FCSTD DOCUMENT  (FreeCAD 0.18R16131 (Git))
Label: Blinds
License: All rights reserved
LicenseURL: http://en.wikipedia.org/wiki/All_rights_reserved
objects: App::Part×2, Sketcher::SketchObject×2
note: 2 computed .brp shape members not serialized (recipe doc carries the construction recipe); baked Part::Feature solids carry a one-line shape summary decoded from their .brp

FEATURE [App::Part] Part
  Origin = -> Origin
FEATURE [Sketcher::SketchObject] Sketch
  sketch-geometry (54):
    g0: LineSegment StartX=-75.9771 StartY=43.0234 StartZ=0 EndX=-55.9771 EndY=43.0234 EndZ=0
    g1: LineSegment StartX=-75.9771 StartY=43.0234 StartZ=0 EndX=-75.9771 EndY=33.0234 EndZ=0
    g2: LineSegment StartX=-55.9771 StartY=43.0234 StartZ=0 EndX=-55.9771 EndY=33.0234 EndZ=0
    g3: LineSegment StartX=-75.9771 StartY=33.0234 StartZ=0 EndX=-85.9771 EndY=33.0234 EndZ=0
    g4: LineSegment StartX=-85.9771 StartY=33.0234 StartZ=0 EndX=-85.9771 EndY=25.0234 EndZ=0
    g5: LineSegment StartX=-35.9771 StartY=33.0234 StartZ=0 EndX=-55.9771 EndY=33.0234 EndZ=0
    g6: Circle CenterX=-71.9771 CenterY=37.6234 CenterZ=0 NormalX=0 NormalY=0 NormalZ=1 AngleXU=0 Radius=1.6
    g7: Circle CenterX=-59.9771 CenterY=37.6234 CenterZ=0 NormalX=0 NormalY=0 NormalZ=1 AngleXU=0 Radius=1.6
    g8: Circle CenterX=-39.9771 CenterY=29.0234 CenterZ=0 NormalX=0 NormalY=0 NormalZ=1 AngleXU=0 Radius=2.2
    g9: LineSegment StartX=-35.9771 StartY=33.0234 StartZ=0 EndX=-35.9771 EndY=29.0234 EndZ=0
    g10: LineSegment StartX=-85.9771 StartY=25.0234 StartZ=0 EndX=-39.9771 EndY=25.0234 EndZ=0
    g11: ArcOfCircle CenterX=-39.9771 CenterY=29.0234 CenterZ=0 NormalX=0 NormalY=0 NormalZ=1 AngleXU=0 Radius=4 StartAngle=4.71239 EndAngle=6.28319
    g12: LineSegment StartX=-29.5565 StartY=104.387 StartZ=0 EndX=-29.5565 EndY=99.3874 EndZ=0
    g13: LineSegment StartX=-29.5565 StartY=104.387 StartZ=0 EndX=-151.456 EndY=104.387 EndZ=0
    g14: LineSegment StartX=-151.456 StartY=104.387 StartZ=0 EndX=-151.456 EndY=101.387 EndZ=0
    g15: LineSegment StartX=-151.456 StartY=101.387 StartZ=0 EndX=-146.456 EndY=101.387 EndZ=0
    g16: LineSegment StartX=-146.456 StartY=101.387 StartZ=0 EndX=-146.456 EndY=98.3874 EndZ=0
    g17: LineSegment StartX=-146.456 StartY=98.3874 StartZ=0 EndX=-154.456 EndY=98.3874 EndZ=0
    g18: LineSegment StartX=-154.456 StartY=98.3874 StartZ=0 EndX=-154.456 EndY=104.387 EndZ=0
    g19: LineSegment StartX=-154.456 StartY=104.387 StartZ=0 EndX=-241.456 EndY=104.387 EndZ=0
    g20: LineSegment StartX=-241.456 StartY=104.387 StartZ=0 EndX=-241.456 EndY=101.387 EndZ=0
    g21: LineSegment StartX=-241.456 StartY=101.387 StartZ=0 EndX=-236.456 EndY=101.387 EndZ=0
    g22: LineSegment StartX=-236.456 StartY=101.387 StartZ=0 EndX=-236.456 EndY=98.3874 EndZ=0
    g23: LineSegment StartX=-236.456 StartY=98.3874 StartZ=0 EndX=-244.456 EndY=98.3874 EndZ=0
    g24: LineSegment StartX=-244.456 StartY=98.3874 StartZ=0 EndX=-244.456 EndY=104.387 EndZ=0
    g25: LineSegment StartX=-244.456 StartY=104.387 StartZ=0 EndX=-359.556 EndY=104.387 EndZ=0
    g26: LineSegment StartX=-359.556 StartY=104.387 StartZ=0 EndX=-359.556 EndY=99.3874 EndZ=0
    g27: LineSegment StartX=-279.556 StartY=39.3874 StartZ=0 EndX=-109.556 EndY=39.3874 EndZ=0
    g28: LineSegment StartX=-241.456 StartY=95.3874 StartZ=0 EndX=-241.456 EndY=85.3874 EndZ=0
    g29: LineSegment StartX=-241.456 StartY=95.3874 StartZ=0 EndX=-244.456 EndY=95.3874 EndZ=0
    g30: LineSegment StartX=-244.456 StartY=95.3874 StartZ=0 EndX=-244.456 EndY=85.3874 EndZ=0
    g31: LineSegment StartX=-241.456 StartY=85.3874 StartZ=0 EndX=-244.456 EndY=85.3874 EndZ=0
    g32: LineSegment StartX=-154.456 StartY=95.3874 StartZ=0 EndX=-154.456 EndY=85.3874 EndZ=0
    g33: LineSegment StartX=-154.456 StartY=95.3874 StartZ=0 EndX=-151.456 EndY=95.3874 EndZ=0
    g34: LineSegment StartX=-151.456 StartY=95.3874 StartZ=0 EndX=-151.456 EndY=85.3874 EndZ=0
    g35: LineSegment StartX=-154.456 StartY=85.3874 StartZ=0 EndX=-151.456 EndY=85.3874 EndZ=0
    g36: Circle CenterX=-276.556 CenterY=42.3874 CenterZ=0 NormalX=0 NormalY=0 NormalZ=1 AngleXU=0 Radius=1.6
    g37: Circle CenterX=-216.556 CenterY=42.3874 CenterZ=0 NormalX=0 NormalY=0 NormalZ=1 AngleXU=0 Radius=1.6
    g38: Circle CenterX=-172.556 CenterY=42.3874 CenterZ=0 NormalX=0 NormalY=0 NormalZ=1 AngleXU=0 Radius=1.6
    g39: Circle CenterX=-112.556 CenterY=42.3874 CenterZ=0 NormalX=0 NormalY=0 NormalZ=1 AngleXU=0 Radius=1.6
    g40: LineSegment StartX=-54.0017 StartY=76.5916 StartZ=0 EndX=-54.0017 EndY=70.5916 EndZ=0
    g41: LineSegment StartX=-54.0017 StartY=76.5916 StartZ=0 EndX=-48.0017 EndY=76.5916 EndZ=0
    g42: LineSegment StartX=-48.0017 StartY=76.5916 StartZ=0 EndX=-48.0017 EndY=57.5916 EndZ=0
    g43: LineSegment StartX=-48.0017 StartY=57.5916 StartZ=0 EndX=-54.0017 EndY=57.5916 EndZ=0
    g44: LineSegment StartX=-54.0017 StartY=57.5916 StartZ=0 EndX=-54.0017 EndY=67.5916 EndZ=0
    g45: LineSegment StartX=-54.0017 StartY=67.5916 StartZ=0 EndX=-51.0017 EndY=67.5916 EndZ=0
    g46: LineSegment StartX=-51.0017 StartY=67.5916 StartZ=0 EndX=-51.0017 EndY=70.5916 EndZ=0
    g47: LineSegment StartX=-51.0017 StartY=70.5916 StartZ=0 EndX=-54.0017 EndY=70.5916 EndZ=0
    g48: LineSegment StartX=-359.556 StartY=99.3874 StartZ=0 EndX=-319.556 EndY=99.3874 EndZ=0
    g49: LineSegment StartX=-279.556 StartY=64.3874 StartZ=0 EndX=-279.556 EndY=39.3874 EndZ=0
    g50: ArcOfCircle CenterX=-319.243 CenterY=59.3886 CenterZ=0 NormalX=0 NormalY=0 NormalZ=1 AngleXU=0 Radius=40 StartAngle=0.125297 EndAngle=1.57864
    g51: LineSegment StartX=-29.5565 StartY=99.3874 StartZ=0 EndX=-69.5565 EndY=99.3874 EndZ=0
    g52: LineSegment StartX=-109.556 StartY=64.3874 StartZ=0 EndX=-109.556 EndY=39.3874 EndZ=0
    g53: ArcOfCircle CenterX=-69.8701 CenterY=59.3886 CenterZ=0 NormalX=0 NormalY=0 NormalZ=1 AngleXU=0 Radius=40 StartAngle=1.56296 EndAngle=3.0163
  constraints (159):
    c: Coincident(g3,g1)
    c: Coincident(g0,g1)
    c: Coincident(g0,g2)
    c: Coincident(g2,g5)
    c: Coincident(g3,g4)
    c: Parallel(g2,g1)
    c: Parallel(g1,g4)
    c: DistanceY(g1,g2) = 0
    c: DistanceY(g4,g4) = 8
    c: DistanceY(g1,g1) = 10
    c: DistanceX(g3,g3) = 10
    c: DistanceX(g5,g5) = 20
    c: DistanceX(g0,g0) = 20
    c: Radius(g6) = 1.6
    c: Equal(g6,g7)
    c: DistanceY(g6,g7) = 0
    c: Radius(g8) = 2.2
    c: DistanceX(g8,g5) = 4
    c: DistanceY(g8,g5) = 4
    c: DistanceY(g1,g6) = 4.6
    c: DistanceX(g1,g6) = 4
    c: DistanceX(g7,g2) = 4
    c: Coincident(g5,g9)
    c: Coincident(g4,g10)
    c: Angle(g10) = 0
    c: Perpendicular(g4,g10)
    c: Parallel(g4,g9)
    c: Coincident(g10,g11)
    c: Parallel(g10,g0)
    c: Parallel(g0,g3)
    c: Parallel(g3,g5)
    c: Coincident(g9,g11)
    c: DistanceY(g9,g9) = 4
    c: DistanceX(g10,g10) = 46
    c: Radius(g11) = 4
    c: Angle(g27) = 0
    c: Coincident(g13,g12)
    c: Coincident(g14,g13)
    c: Coincident(g14,g15)
    c: Coincident(g15,g16)
    c: Coincident(g16,g17)
    c: Coincident(g18,g17)
    c: Coincident(g18,g19)
    c: Coincident(g20,g19)
    c: Coincident(g20,g21)
    c: Coincident(g21,g22)
    c: Coincident(g23,g22)
    c: Coincident(g23,g24)
    c: Coincident(g24,g25)
    c: Coincident(g25,g26)
    c: Coincident(g29,g28)
    c: Coincident(g29,g30)
    c: Coincident(g31,g30)
    c: Coincident(g31,g28)
    c: Coincident(g35,g32)
    c: Coincident(g35,g34)
    c: Coincident(g33,g32)
    c: Coincident(g33,g34)
    c: Perpendicular(g12,g27)
    c: Parallel(g27,g35)
    c: Parallel(g35,g33)
    c: Parallel(g33,g31)
    c: Parallel(g31,g29)
    c: Parallel(g29,g17)
    c: Parallel(g17,g15)
    c: Parallel(g15,g13)
    c: Parallel(g13,g19)
    c: Parallel(g19,g23)
    c: Parallel(g23,g21)
    c: Parallel(g21,g25)
    c: Parallel(g12,g34)
    c: Parallel(g34,g32)
    c: Parallel(g32,g16)
    c: Parallel(g16,g14)
    c: Parallel(g14,g18)
    c: Parallel(g18,g22)
    c: Parallel(g22,g20)
    c: Parallel(g20,g24)
    c: Parallel(g24,g30)
    c: Parallel(g30,g28)
    c: Parallel(g28,g26)
    c: DistanceX(g27,g12) = 80
    c: DistanceX(g26,g27) = 80
    c: DistanceX(g25,g12) = 330
    c: DistanceY(g12,g12) = 5
    c: DistanceY(g26,g26) = 5
    c: DistanceY(g24,g19) = 0
    c: DistanceY(g18,g13) = 0
    c: DistanceY(g20,g20) = 3
    c: DistanceY(g14,g14) = 3
    c: DistanceX(g15,g15) = 5
    c: DistanceX(g21,g21) = 5
    c: DistanceY(g22,g22) = 3
    c: DistanceY(g16,g16) = 3
    c: DistanceX(g17,g17) = 8
    c: DistanceX(g23,g23) = 8
    c: DistanceX(g22,g16) = 90
    c: DistanceX(g29,g29) = 3
    c: DistanceY(g28,g28) = 10
    c: DistanceX(g20,g28) = 0
    c: DistanceX(g33,g33) = 3
    c: DistanceY(g34,g34) = 10
    c: DistanceX(g14,g33) = 0
    c: DistanceY(g32,g17) = 3
    c: DistanceY(g29,g23) = 3
    c: DistanceY(g27,g25) = 65
    c: Radius(g36) = 1.6
    c: Equal(g36,g37)
    c: Equal(g37,g38)
    c: Equal(g38,g39)
    c: DistanceY(g27,g36) = 3
    c: DistanceY(g36,g37) = 0
    c: DistanceY(g37,g38) = 0
    c: DistanceY(g38,g39) = 0
    c: DistanceX(g27,g36) = 3
    c: DistanceX(g39,g27) = 3
    c: DistanceX(g36,g37) = 60
    c: DistanceX(g38,g39) = 60
    c: Coincident(g43,g44)
    c: Coincident(g43,g42)
    c: Coincident(g45,g44)
    c: Coincident(g46,g45)
    c: Coincident(g46,g47)
    c: Coincident(g40,g47)
    c: Coincident(g41,g40)
    c: Coincident(g41,g42)
    c: Angle(g43) = 3.14159
    c: Perpendicular(g42,g43)
    c: Parallel(g43,g45)
    c: Parallel(g45,g47)
    c: Parallel(g47,g41)
    c: Parallel(g42,g44)
    c: Parallel(g44,g46)
    c: Parallel(g46,g40)
    c: DistanceY(g44,g44) = 10
    c: DistanceY(g46,g46) = 3
    c: DistanceY(g40,g40) = 6
    c: DistanceX(g41,g41) = 6
    c: DistanceX(g47,g47) = 3
    c: DistanceX(g44,g40) = 0
    c: DistanceX(g25,g22) = 123.1
    c: Parallel(g27,g48)
    c: Coincident(g26,g48)
    c: DistanceX(g48,g48) = 40
    c: Parallel(g12,g49)
    c: Coincident(g27,g49)
    c: DistanceY(g49,g49) = 25
    c: Coincident(g48,g50)
    c: Coincident(g49,g50)
    c: Radius(g50) = 40
    c: Parallel(g12,g52)
    c: Parallel(g27,g51)
    c: Coincident(g27,g52)
    c: Coincident(g12,g51)
    c: DistanceX(g51,g51) = 40
    c: DistanceY(g52,g52) = 25
    c: Coincident(g51,g53)
    c: Coincident(g52,g53)
    c: Radius(g53) = 40
FEATURE [App::Part] Part001
  Origin = -> Origin001
FEATURE [Sketcher::SketchObject] Sketch001
  sketch-geometry (94):
    g0: LineSegment StartX=-140.392 StartY=244.588 StartZ=0 EndX=-134.392 EndY=244.588 EndZ=0
    g1: LineSegment StartX=-134.392 StartY=244.588 StartZ=0 EndX=-134.392 EndY=234.588 EndZ=0
    g2: LineSegment StartX=-134.392 StartY=234.588 StartZ=0 EndX=-137.392 EndY=234.588 EndZ=0
    g3: LineSegment StartX=-137.392 StartY=234.588 StartZ=0 EndX=-137.392 EndY=231.588 EndZ=0
    g4: LineSegment StartX=-137.392 StartY=231.588 StartZ=0 EndX=-138.937 EndY=229.016 EndZ=0
    g5: LineSegment StartX=-138.937 StartY=229.016 StartZ=0 EndX=-136.366 EndY=227.471 EndZ=0
    g6: LineSegment StartX=-136.366 StartY=227.471 StartZ=0 EndX=-141.516 EndY=218.9 EndZ=0
    g7: LineSegment StartX=-141.516 StartY=218.9 StartZ=0 EndX=-146.659 EndY=221.99 EndZ=0
    g8: LineSegment StartX=-146.659 StartY=221.99 StartZ=0 EndX=-140.392 EndY=244.588 EndZ=0
    g9: LineSegment StartX=-270.145 StartY=249.774 StartZ=0 EndX=-170.145 EndY=249.774 EndZ=0
    g10: LineSegment StartX=-170.145 StartY=249.774 StartZ=0 EndX=-170.145 EndY=209.774 EndZ=0
    g11: LineSegment StartX=-170.145 StartY=209.774 StartZ=0 EndX=-270.145 EndY=209.774 EndZ=0
    g12: LineSegment StartX=-270.145 StartY=209.774 StartZ=0 EndX=-270.145 EndY=249.774 EndZ=0
    g13: LineSegment StartX=-236.595 StartY=247.774 StartZ=0 EndX=-233.595 EndY=247.774 EndZ=0
    g14: LineSegment StartX=-233.595 StartY=247.774 StartZ=0 EndX=-233.595 EndY=237.774 EndZ=0
    g15: LineSegment StartX=-233.595 StartY=237.774 StartZ=0 EndX=-236.595 EndY=237.774 EndZ=0
    g16: LineSegment StartX=-236.595 StartY=237.774 StartZ=0 EndX=-236.595 EndY=247.774 EndZ=0
    g17: LineSegment StartX=-206.695 StartY=247.774 StartZ=0 EndX=-203.695 EndY=247.774 EndZ=0
    g18: LineSegment StartX=-203.695 StartY=247.774 StartZ=0 EndX=-203.695 EndY=237.774 EndZ=0
    g19: LineSegment StartX=-203.695 StartY=237.774 StartZ=0 EndX=-206.695 EndY=237.774 EndZ=0
    g20: LineSegment StartX=-206.695 StartY=237.774 StartZ=0 EndX=-206.695 EndY=247.774 EndZ=0
    g21: LineSegment StartX=-267.145 StartY=242.774 StartZ=0 EndX=-257.145 EndY=242.774 EndZ=0
    g22: LineSegment StartX=-257.145 StartY=242.774 StartZ=0 EndX=-257.145 EndY=239.774 EndZ=0
    g23: LineSegment StartX=-257.145 StartY=239.774 StartZ=0 EndX=-267.145 EndY=239.774 EndZ=0
    g24: LineSegment StartX=-267.145 StartY=239.774 StartZ=0 EndX=-267.145 EndY=242.774 EndZ=0
    g25: LineSegment StartX=-267.145 StartY=219.774 StartZ=0 EndX=-257.145 EndY=219.774 EndZ=0
    g26: LineSegment StartX=-257.145 StartY=219.774 StartZ=0 EndX=-257.145 EndY=216.774 EndZ=0
    g27: LineSegment StartX=-257.145 StartY=216.774 StartZ=0 EndX=-267.145 EndY=216.774 EndZ=0
    g28: LineSegment StartX=-267.145 StartY=216.774 StartZ=0 EndX=-267.145 EndY=219.774 EndZ=0
    g29: LineSegment StartX=-183.145 StartY=242.774 StartZ=0 EndX=-173.145 EndY=242.774 EndZ=0
    g30: LineSegment StartX=-173.145 StartY=242.774 StartZ=0 EndX=-173.145 EndY=239.774 EndZ=0
    g31: LineSegment StartX=-173.145 StartY=239.774 StartZ=0 EndX=-183.145 EndY=239.774 EndZ=0
    g32: LineSegment StartX=-183.145 StartY=239.774 StartZ=0 EndX=-183.145 EndY=242.774 EndZ=0
    g33: LineSegment StartX=-183.145 StartY=219.774 StartZ=0 EndX=-173.145 EndY=219.774 EndZ=0
    g34: LineSegment StartX=-173.145 StartY=219.774 StartZ=0 EndX=-173.145 EndY=216.774 EndZ=0
    g35: LineSegment StartX=-173.145 StartY=216.774 StartZ=0 EndX=-183.145 EndY=216.774 EndZ=0
    g36: LineSegment StartX=-183.145 StartY=216.774 StartZ=0 EndX=-183.145 EndY=219.774 EndZ=0
    g37: LineSegment StartX=-353.959 StartY=249.229 StartZ=0 EndX=-297.959 EndY=249.229 EndZ=0
    g38: LineSegment StartX=-297.959 StartY=249.229 StartZ=0 EndX=-297.959 EndY=209.229 EndZ=0
    g39: LineSegment StartX=-297.959 StartY=209.229 StartZ=0 EndX=-353.959 EndY=209.229 EndZ=0
    g40: LineSegment StartX=-353.959 StartY=209.229 StartZ=0 EndX=-353.959 EndY=249.229 EndZ=0
    g41: LineSegment StartX=-310.959 StartY=242.229 StartZ=0 EndX=-300.959 EndY=242.229 EndZ=0
    g42: LineSegment StartX=-300.959 StartY=242.229 StartZ=0 EndX=-300.959 EndY=239.229 EndZ=0
    g43: LineSegment StartX=-300.959 StartY=239.229 StartZ=0 EndX=-310.959 EndY=239.229 EndZ=0
    g44: LineSegment StartX=-310.959 StartY=239.229 StartZ=0 EndX=-310.959 EndY=242.229 EndZ=0
    g45: LineSegment StartX=-310.959 StartY=219.229 StartZ=0 EndX=-300.959 EndY=219.229 EndZ=0
    g46: LineSegment StartX=-300.959 StartY=219.229 StartZ=0 EndX=-300.959 EndY=216.229 EndZ=0
    g47: LineSegment StartX=-300.959 StartY=216.229 StartZ=0 EndX=-310.959 EndY=216.229 EndZ=0
    g48: LineSegment StartX=-310.959 StartY=216.229 StartZ=0 EndX=-310.959 EndY=219.229 EndZ=0
    g49: LineSegment StartX=-79.5319 StartY=246.61 StartZ=0 EndX=-59.5319 EndY=246.61 EndZ=0
    g50: LineSegment StartX=-79.5319 StartY=246.61 StartZ=0 EndX=-79.5319 EndY=236.61 EndZ=0
    g51: LineSegment StartX=-79.5319 StartY=236.61 StartZ=0 EndX=-89.5319 EndY=236.61 EndZ=0
    g52: LineSegment StartX=-89.5319 StartY=236.61 StartZ=0 EndX=-89.5319 EndY=231.61 EndZ=0
    g53: LineSegment StartX=-59.5319 StartY=246.61 StartZ=0 EndX=-59.5319 EndY=236.61 EndZ=0
    g54: LineSegment StartX=-59.5319 StartY=236.61 StartZ=0 EndX=-56.5319 EndY=236.61 EndZ=0
    g55: LineSegment StartX=-56.5319 StartY=236.61 StartZ=0 EndX=-56.5319 EndY=233.61 EndZ=0
    g56: LineSegment StartX=-56.5319 StartY=233.61 StartZ=0 EndX=-67.5319 EndY=233.61 EndZ=0
    g57: LineSegment StartX=-67.5319 StartY=233.61 StartZ=0 EndX=-67.5319 EndY=230.61 EndZ=0
    g58: LineSegment StartX=-67.5319 StartY=230.61 StartZ=0 EndX=-64.5319 EndY=230.61 EndZ=0
    g59: LineSegment StartX=-64.5319 StartY=230.61 StartZ=0 EndX=-64.5319 EndY=220.61 EndZ=0
    g60: LineSegment StartX=-64.5319 StartY=220.61 StartZ=0 EndX=-69.5319 EndY=220.61 EndZ=0
    g61: LineSegment StartX=-69.5319 StartY=220.61 StartZ=0 EndX=-89.5319 EndY=231.61 EndZ=0
    g62: Circle CenterX=-75.5319 CenterY=241.21 CenterZ=0 NormalX=0 NormalY=0 NormalZ=1 AngleXU=0 Radius=1.6
    g63: Circle CenterX=-63.5319 CenterY=241.21 CenterZ=0 NormalX=0 NormalY=0 NormalZ=1 AngleXU=0 Radius=1.6
    g64: LineSegment StartX=-335.237 StartY=314.758 StartZ=0 EndX=-299.237 EndY=314.758 EndZ=0
    g65: LineSegment StartX=-299.237 StartY=314.758 StartZ=0 EndX=-299.237 EndY=274.758 EndZ=0
    g66: LineSegment StartX=-299.237 StartY=274.758 StartZ=0 EndX=-319.237 EndY=274.758 EndZ=0
    g67: LineSegment StartX=-335.237 StartY=314.758 StartZ=0 EndX=-335.237 EndY=304.758 EndZ=0
    g68: LineSegment StartX=-335.237 StartY=304.758 StartZ=0 EndX=-355.237 EndY=304.758 EndZ=0
    g69: LineSegment StartX=-355.237 StartY=304.758 StartZ=0 EndX=-355.237 EndY=301.758 EndZ=0
    g70: ArcOfCircle CenterX=-353.323 CenterY=266.811 CenterZ=0 NormalX=0 NormalY=0 NormalZ=1 AngleXU=0 Radius=35 StartAngle=0.229073 EndAngle=1.62552
    g71: LineSegment StartX=-312.237 StartY=307.758 StartZ=0 EndX=-302.237 EndY=307.758 EndZ=0
    g72: LineSegment StartX=-302.237 StartY=307.758 StartZ=0 EndX=-302.237 EndY=304.758 EndZ=0
    g73: LineSegment StartX=-302.237 StartY=304.758 StartZ=0 EndX=-312.237 EndY=304.758 EndZ=0
    g74: LineSegment StartX=-312.237 StartY=304.758 StartZ=0 EndX=-312.237 EndY=307.758 EndZ=0
    g75: LineSegment StartX=-312.237 StartY=284.758 StartZ=0 EndX=-302.237 EndY=284.758 EndZ=0
    g76: LineSegment StartX=-302.237 StartY=284.758 StartZ=0 EndX=-302.237 EndY=281.758 EndZ=0
    g77: LineSegment StartX=-302.237 StartY=281.758 StartZ=0 EndX=-312.237 EndY=281.758 EndZ=0
    g78: LineSegment StartX=-312.237 StartY=281.758 StartZ=0 EndX=-312.237 EndY=284.758 EndZ=0
    g79: LineSegment StartX=-81.0249 StartY=284.242 StartZ=0 EndX=-61.0249 EndY=284.242 EndZ=0
    g80: LineSegment StartX=-81.0249 StartY=284.242 StartZ=0 EndX=-81.0249 EndY=274.242 EndZ=0
    g81: LineSegment StartX=-81.0249 StartY=274.242 StartZ=0 EndX=-91.0249 EndY=274.242 EndZ=0
    g82: LineSegment StartX=-91.0249 StartY=274.242 StartZ=0 EndX=-91.0249 EndY=269.242 EndZ=0
    g83: LineSegment StartX=-61.0249 StartY=284.242 StartZ=0 EndX=-61.0249 EndY=274.242 EndZ=0
    g84: LineSegment StartX=-61.0249 StartY=274.242 StartZ=0 EndX=-58.0249 EndY=274.242 EndZ=0
    g85: LineSegment StartX=-58.0249 StartY=274.242 StartZ=0 EndX=-58.0249 EndY=271.242 EndZ=0
    g86: LineSegment StartX=-58.0249 StartY=271.242 StartZ=0 EndX=-61.0249 EndY=271.242 EndZ=0
    g87: LineSegment StartX=-61.0249 StartY=271.242 StartZ=0 EndX=-61.0249 EndY=268.242 EndZ=0
    g88: LineSegment StartX=-61.0249 StartY=268.242 StartZ=0 EndX=-58.0249 EndY=268.242 EndZ=0
    g89: LineSegment StartX=-58.0249 StartY=268.242 StartZ=0 EndX=-58.0249 EndY=258.242 EndZ=0
    g90: LineSegment StartX=-58.0249 StartY=258.242 StartZ=0 EndX=-63.0249 EndY=258.242 EndZ=0
    g91: LineSegment StartX=-63.0249 StartY=258.242 StartZ=0 EndX=-91.0249 EndY=269.242 EndZ=0
    g92: Circle CenterX=-77.0249 CenterY=278.842 CenterZ=0 NormalX=0 NormalY=0 NormalZ=1 AngleXU=0 Radius=1.6
    g93: Circle CenterX=-65.0249 CenterY=278.842 CenterZ=0 NormalX=0 NormalY=0 NormalZ=1 AngleXU=0 Radius=1.6
  constraints (271):
    c: Coincident(g0,g1)
    c: Coincident(g2,g1)
    c: Coincident(g2,g3)
    c: Coincident(g3,g4)
    c: Coincident(g5,g4)
    c: Coincident(g5,g6)
    c: Coincident(g7,g6)
    c: Coincident(g7,g8)
    c: Coincident(g0,g8)
    c: Angle(g2) = 3.14159
    c: Perpendicular(g1,g2)
    c: Parallel(g2,g0)
    c: Parallel(g1,g3)
    c: Angle(g3,g4) = 2.60054
    c: Parallel(g4,g6)
    c: Perpendicular(g5,g4)
    c: Parallel(g5,g7)
    c: DistanceX(g2,g2) = 3
    c: DistanceY(g1,g1) = 10
    c: DistanceY(g3,g3) = 3
    c: Distance(g5) = 3
    c: Distance(g4) = 3
    c: Distance(g6) = 10
    c: Distance(g7) = 6
    c: Distance(g0) = 6
    c: Coincident(g9,g10)
    c: Coincident(g10,g11)
    c: Coincident(g11,g12)
    c: Coincident(g12,g9)
    c: Horizontal(g9)
    c: Horizontal(g11)
    c: Vertical(g10)
    c: Vertical(g12)
    c: Coincident(g13,g14)
    c: Coincident(g14,g15)
    c: Coincident(g15,g16)
    c: Coincident(g16,g13)
    c: Horizontal(g13)
    c: Horizontal(g15)
    c: Vertical(g14)
    c: Vertical(g16)
    c: Coincident(g17,g18)
    c: Coincident(g18,g19)
    c: Coincident(g19,g20)
    c: Coincident(g20,g17)
    c: Horizontal(g17)
    c: Horizontal(g19)
    c: Vertical(g18)
    c: Vertical(g20)
    c: Coincident(g21,g22)
    c: Coincident(g22,g23)
    c: Coincident(g23,g24)
    c: Coincident(g24,g21)
    c: Horizontal(g21)
    c: Horizontal(g23)
    c: Vertical(g22)
    c: Vertical(g24)
    c: Coincident(g25,g26)
    c: Coincident(g26,g27)
    c: Coincident(g27,g28)
    c: Coincident(g28,g25)
    c: Horizontal(g25)
    c: Horizontal(g27)
    c: Vertical(g26)
    c: Vertical(g28)
    c: Coincident(g29,g30)
    c: Coincident(g30,g31)
    c: Coincident(g31,g32)
    c: Coincident(g32,g29)
    c: Horizontal(g29)
    c: Horizontal(g31)
    c: Vertical(g30)
    c: Vertical(g32)
    c: Coincident(g33,g34)
    c: Coincident(g34,g35)
    c: Coincident(g35,g36)
    c: Coincident(g36,g33)
    c: Horizontal(g33)
    c: Horizontal(g35)
    c: Vertical(g34)
    c: Vertical(g36)
    c: Coincident(g37,g38)
    c: Coincident(g38,g39)
    c: Coincident(g39,g40)
    c: Coincident(g40,g37)
    c: Horizontal(g37)
    c: Horizontal(g39)
    c: Vertical(g38)
    c: Vertical(g40)
    c: Coincident(g41,g42)
    c: Coincident(g42,g43)
    c: Coincident(g43,g44)
    c: Coincident(g44,g41)
    c: Horizontal(g41)
    c: Horizontal(g43)
    c: Vertical(g42)
    c: Vertical(g44)
    c: Coincident(g45,g46)
    c: Coincident(g46,g47)
    c: Coincident(g47,g48)
    c: Coincident(g48,g45)
    c: Horizontal(g45)
    c: Horizontal(g47)
    c: Vertical(g46)
    c: Vertical(g48)
    c: DistanceX(g11,g11) = 100
    c: DistanceY(g24,g24) = 3
    c: DistanceX(g21,g21) = 10
    c: DistanceX(g25,g25) = 10
    c: DistanceY(g28,g28) = 3
    c: DistanceX(g29,g29) = 10
    c: DistanceY(g32,g32) = 3
    c: DistanceX(g33,g33) = 10
    c: DistanceY(g36,g36) = 3
    c: DistanceX(g25,g22) = 0
    c: DistanceX(g31,g33) = 0
    c: DistanceX(g13,g13) = 3
    c: DistanceX(g17,g17) = 3
    c: DistanceY(g16,g16) = 10
    c: DistanceY(g20,g20) = 10
    c: DistanceY(g13,g17) = 0
    c: DistanceY(g12,g12) = 40
    c: DistanceX(g11,g27) = 3
    c: DistanceX(g34,g10) = 3
    c: DistanceY(g17,g9) = 2
    c: DistanceX(g13,g17) = 26.9
    c: DistanceX(g9,g13) = 36.55
    c: DistanceY(g25,g22) = 20
    c: DistanceY(g11,g25) = 10
    c: DistanceY(g33,g30) = 20
    c: DistanceY(g10,g33) = 10
    c: DistanceY(g46,g46) = 3
    c: DistanceY(g42,g42) = 3
    c: DistanceX(g43,g43) = 10
    c: DistanceX(g45,g45) = 10
    c: DistanceX(g42,g45) = 0
    c: DistanceY(g45,g42) = 20
    c: DistanceX(g46,g38) = 3
    c: DistanceY(g38,g45) = 10
    c: DistanceY(g38,g38) = 40
    c: DistanceX(g39,g39) = 56
    c: Angle(g49) = 0
    c: Coincident(g49,g53)
    c: Coincident(g54,g53)
    c: Coincident(g55,g54)
    c: Coincident(g55,g56)
    c: Coincident(g56,g57)
    c: Coincident(g58,g57)
    c: Coincident(g58,g59)
    c: Coincident(g60,g59)
    c: Coincident(g61,g60)
    c: Coincident(g52,g61)
    c: Coincident(g51,g52)
    c: Coincident(g51,g50)
    c: Coincident(g49,g50)
    c: Perpendicular(g53,g49)
    c: Parallel(g49,g54)
    c: Parallel(g54,g56)
    c: Parallel(g56,g58)
    c: Parallel(g58,g60)
    c: Parallel(g60,g51)
    c: Parallel(g53,g55)
    c: Parallel(g55,g57)
    c: Parallel(g57,g59)
    c: Parallel(g59,g52)
    c: Parallel(g52,g50)
    c: DistanceX(g49,g49) = 20
    c: DistanceY(g53,g53) = 10
    c: DistanceY(g50,g53) = 0
    c: DistanceX(g54,g54) = 3
    c: DistanceY(g55,g55) = 3
    c: DistanceX(g58,g58) = 3
    c: DistanceY(g57,g57) = 3
    c: DistanceY(g59,g59) = 10
    c: DistanceX(g60,g60) = 5
    c: DistanceX(g51,g51) = 10
    c: DistanceY(g52,g52) = 5
    c: DistanceX(g56,g53) = 8
    c: Radius(g62) = 1.6
    c: Equal(g62,g63)
    c: DistanceY(g62,g63) = 0
    c: DistanceY(g50,g62) = 4.6
    c: DistanceX(g50,g62) = 4
    c: DistanceX(g63,g53) = 4
    c: Angle(g66) = -3.14159
    c: Coincident(g66,g65)
    c: Coincident(g64,g65)
    c: Coincident(g67,g64)
    c: Coincident(g68,g67)
    c: Coincident(g68,g69)
    c: Coincident(g69,g70)
    c: Coincident(g66,g70)
    c: Perpendicular(g65,g66)
    c: Parallel(g66,g64)
    c: Parallel(g64,g68)
    c: Parallel(g65,g67)
    c: Parallel(g67,g69)
    c: DistanceY(g65,g65) = 40
    c: DistanceX(g66,g66) = 20
    c: DistanceX(g68,g64) = 56
    c: DistanceX(g68,g68) = 20
    c: DistanceY(g69,g69) = 3
    c: DistanceY(g67,g67) = 10
    c: Radius(g70) = 35
    c: Coincident(g71,g72)
    c: Coincident(g72,g73)
    c: Coincident(g73,g74)
    c: Coincident(g74,g71)
    c: Horizontal(g71)
    c: Horizontal(g73)
    c: Vertical(g72)
    c: Vertical(g74)
    c: Coincident(g75,g76)
    c: Coincident(g76,g77)
    c: Coincident(g77,g78)
    c: Coincident(g78,g75)
    c: Horizontal(g75)
    c: Horizontal(g77)
    c: Vertical(g76)
    c: Vertical(g78)
    c: DistanceY(g72,g72) = 3
    c: DistanceY(g76,g76) = 3
    c: DistanceX(g71,g71) = 10
    c: DistanceX(g75,g75) = 10
    c: DistanceX(g72,g75) = 0
    c: DistanceY(g75,g72) = 20
    c: DistanceY(g65,g75) = 10
    c: DistanceX(g75,g65) = 3
    c: Angle(g79) = 0
    c: Coincident(g79,g83)
    c: Coincident(g83,g84)
    c: Coincident(g84,g85)
    c: Coincident(g86,g85)
    c: Coincident(g86,g87)
    c: Coincident(g88,g87)
    c: Coincident(g88,g89)
    c: Coincident(g90,g89)
    c: Coincident(g90,g91)
    c: Coincident(g82,g91)
    c: Coincident(g82,g81)
    c: Coincident(g81,g80)
    c: Coincident(g80,g79)
    c: Perpendicular(g83,g79)
    c: Parallel(g79,g81)
    c: Parallel(g81,g90)
    c: Parallel(g90,g88)
    c: Parallel(g88,g86)
    c: Parallel(g86,g84)
    c: Parallel(g83,g80)
    c: Parallel(g80,g82)
    c: Parallel(g82,g85)
    c: Parallel(g85,g87)
    c: Parallel(g87,g89)
    c: Radius(g92) = 1.6
    c: Equal(g92,g93)
    c: DistanceY(g92,g93) = 0
    c: DistanceX(g79,g79) = 20
    c: DistanceX(g84,g84) = 3
    c: DistanceX(g88,g88) = 3
    c: DistanceX(g88,g85) = 0
    c: DistanceY(g85,g85) = 3
    c: DistanceY(g87,g87) = 3
    c: DistanceY(g89,g89) = 10
    c: DistanceY(g83,g80) = 0
    c: DistanceY(g82,g82) = 5
    c: DistanceX(g90,g90) = 5
    c: DistanceY(g83,g83) = 10
    c: DistanceY(g80,g92) = 4.6
    c: DistanceX(g80,g92) = 4
    c: DistanceX(g93,g83) = 4
    c: DistanceX(g81,g81) = 10
